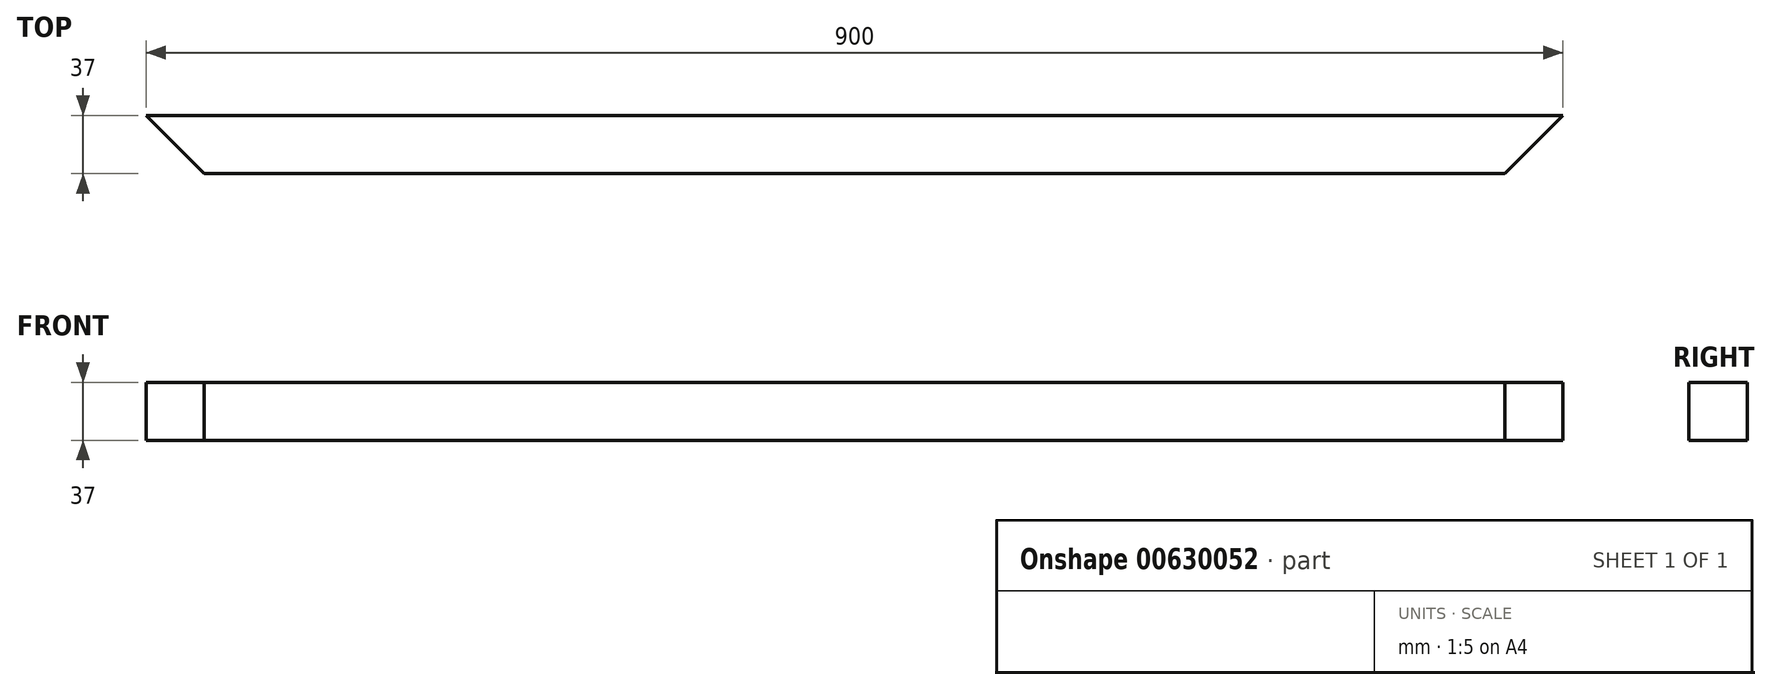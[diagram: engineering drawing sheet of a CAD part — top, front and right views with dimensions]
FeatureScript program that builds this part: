
annotation { "Feature Type Name" : "Feature", "Feature Type Description" : "" }
export const myFeature = defineFeature(function(context is Context, id is Id, definition is map)
    precondition{}
    {
        {
            var Q0;
            Q0=qCreatedBy(makeId("Right.planeOp"),FACE);
            var sketch = newSketch(context, id + "F0", { "sketchPlane" : qUnion([Q0])});
            skLineSegment(sketch, "E0.bottom", {"start": v(0, 0) * mm, "end": v(40, 0) * mm});
            skLineSegment(sketch, "E0.top", {"start": v(0, 40) * mm, "end": v(40, 40) * mm});
            skLineSegment(sketch, "E0.left", {"start": v(0, 0) * mm, "end": v(0, 40) * mm});
            skLineSegment(sketch, "E0.right", {"start": v(40, 0) * mm, "end": v(40, 40) * mm});
            skLineSegment(sketch, "E1.bottom", {"start": v(0, 0) * mm, "end": v(37, 0) * mm});
            skLineSegment(sketch, "E1.top", {"start": v(0, 37) * mm, "end": v(37, 37) * mm});
            skLineSegment(sketch, "E1.left", {"start": v(0, 0) * mm, "end": v(0, 37) * mm});
            skLineSegment(sketch, "E1.right", {"start": v(37, 0) * mm, "end": v(37, 37) * mm});
            skSolve(sketch);
        }
        {
            var Q0;
            Q0=makeQuery(id+"F0.imprint","IMPRINT",FACE,{"disambiguationData":[TD([[makeQuery(id+"F0.imprint","IMPRINT",EDGE,{"derivedFrom":sQuery(id+"F0.wireOp",EDGE,"E0.bottom")}),1.0]])]});
            extrude(context, id + "F1", {"entities" : qUnion([Q0]), "depth" : 900 * mm, "offsetDistance" : 25 * mm});
        }
        {
            var Q0;
            Q0=makeQuery(id+"F1.opExtrude","CAP_EDGE",EDGE,{"disambiguationData":[OSD([sQuery(id+"F0.wireOp",EDGE,"E0.left")])],"isStart":false});
            chamfer(context, id + "F2", {"entities" : qUnion([Q0]), "width" : 37 * mm, "tangentPropagation" : true});
        }
        {
            var Q0;
            Q0=makeQuery(id+"F1.opExtrude","CAP_EDGE",EDGE,{"disambiguationData":[OSD([sQuery(id+"F0.wireOp",EDGE,"E0.left")])],"isStart":true});
            chamfer(context, id + "F3", {"entities" : qUnion([Q0]), "width" : 37 * mm, "tangentPropagation" : true});
        }
    });
